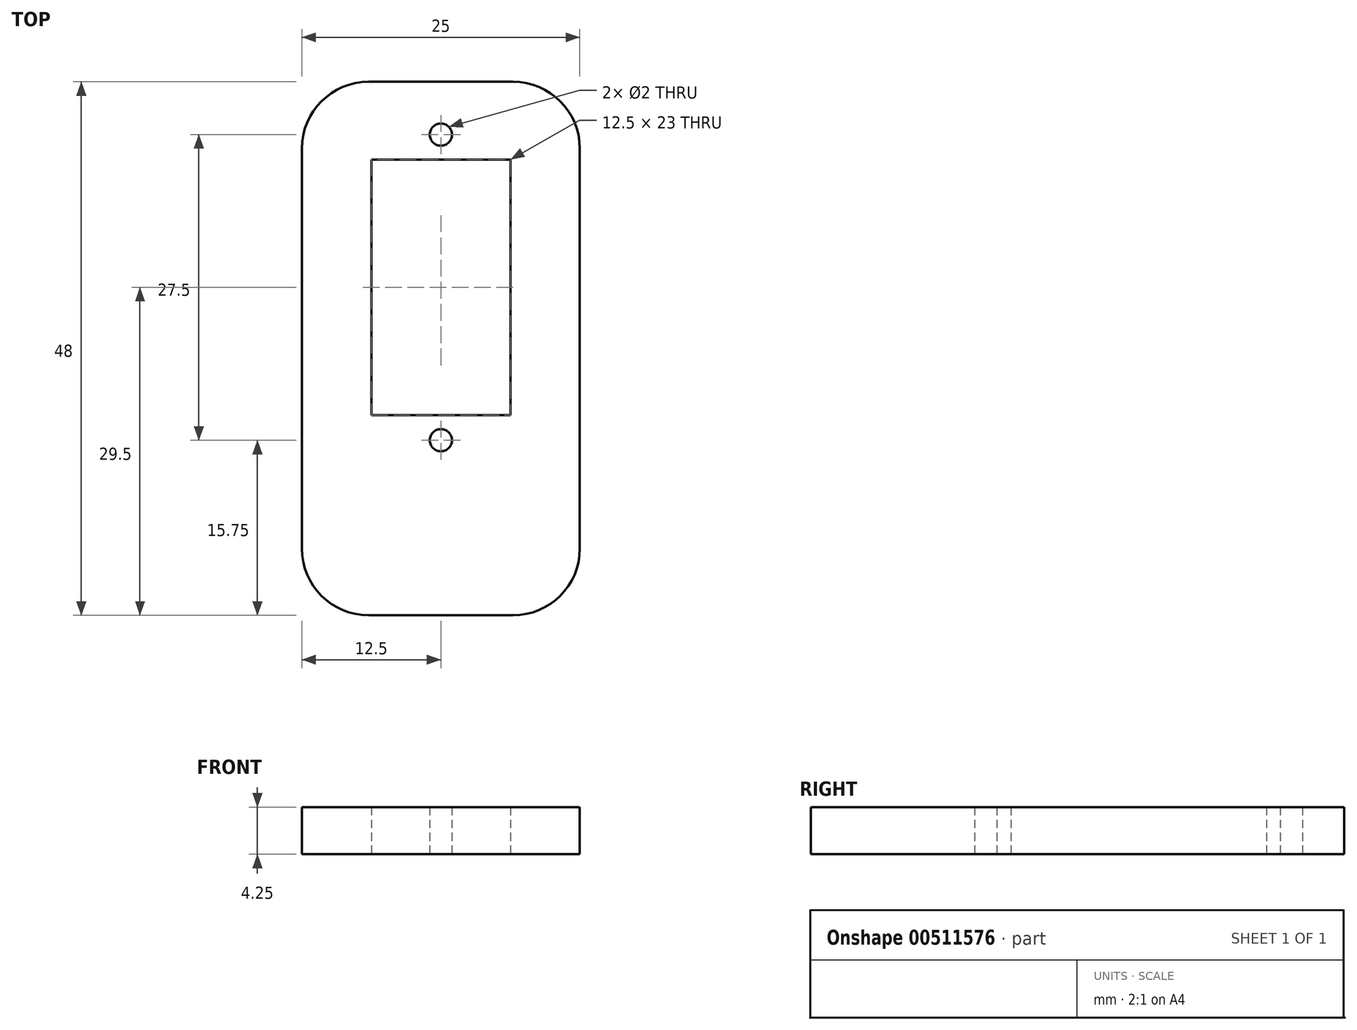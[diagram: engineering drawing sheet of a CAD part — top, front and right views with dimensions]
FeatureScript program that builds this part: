
annotation { "Feature Type Name" : "Feature", "Feature Type Description" : "" }
export const myFeature = defineFeature(function(context is Context, id is Id, definition is map)
    precondition{}
    {
        {
            var Q0;
            Q0=qCreatedBy(makeId("Top.planeOp"),FACE);
            var sketch = newSketch(context, id + "F0", { "sketchPlane" : qUnion([Q0])});
            skLineSegment(sketch, "E0.bottom", {"start": v(6.25, -11.5) * mm, "end": v(-6.25, -11.5) * mm});
            skLineSegment(sketch, "E0.top", {"start": v(6.25, 11.5) * mm, "end": v(-6.25, 11.5) * mm});
            skLineSegment(sketch, "E0.left", {"start": v(6.25, -11.5) * mm, "end": v(6.25, 11.5) * mm});
            skLineSegment(sketch, "E0.right", {"start": v(-6.25, -11.5) * mm, "end": v(-6.25, 11.5) * mm});
            skPoint(sketch, "E0.middle", {"position": v(0, 0) * mm});
            skLineSegment(sketch, "E1.bottom", {"start": v(12.5, -29.5) * mm, "end": v(-12.5, -29.5) * mm});
            skLineSegment(sketch, "E1.top", {"start": v(12.5, 18.5) * mm, "end": v(-12.5, 18.5) * mm});
            skLineSegment(sketch, "E1.left", {"start": v(12.5, -29.5) * mm, "end": v(12.5, 18.5) * mm});
            skLineSegment(sketch, "E1.right", {"start": v(-12.5, -29.5) * mm, "end": v(-12.5, 18.5) * mm});
            skPoint(sketch, "E1.middle", {"position": v(0, -5.5) * mm});
            skLineSegment(sketch, "E2", {"start": v(0, 13.75) * mm, "end": v(0, -13.75) * mm, "construction": true});
            skCircle(sketch, "E3", {"center": v(0, 13.75) * mm, "radius": 1 * mm});
            skCircle(sketch, "E4", {"center": v(0, -13.75) * mm, "radius": 1 * mm});
            skSolve(sketch);
        }
        {
            var Q0;
            Q0=makeQuery(id+"F0.imprint","IMPRINT",FACE,{"disambiguationData":[TD([[makeQuery(id+"F0.imprint","IMPRINT",EDGE,{"derivedFrom":sQuery(id+"F0.wireOp",EDGE,"E0.bottom")}),1.0]])]});
            extrude(context, id + "F1", {"entities" : qUnion([Q0]), "depth" : 4.25 * mm});
        }
        {
            var Q0;
            Q0=makeQuery(id+"F1.opExtrude","SWEPT_EDGE",EDGE,{"disambiguationData":[OSD([sQuery(id+"F0.wireOp",EDGE,"E1.top"),sQuery(id+"F0.wireOp",EDGE,"E1.right")])]});
            var Q1;
            Q1=makeQuery(id+"F1.opExtrude","SWEPT_EDGE",EDGE,{"disambiguationData":[OSD([sQuery(id+"F0.wireOp",EDGE,"E1.top"),sQuery(id+"F0.wireOp",EDGE,"E1.left")])]});
            var Q2;
            Q2=makeQuery(id+"F1.opExtrude","SWEPT_EDGE",EDGE,{"disambiguationData":[OSD([sQuery(id+"F0.wireOp",EDGE,"E1.bottom"),sQuery(id+"F0.wireOp",EDGE,"E1.left")])]});
            var Q3;
            Q3=makeQuery(id+"F1.opExtrude","SWEPT_EDGE",EDGE,{"disambiguationData":[OSD([sQuery(id+"F0.wireOp",EDGE,"E1.bottom"),sQuery(id+"F0.wireOp",EDGE,"E1.right")])]});
            fillet(context, id + "F2", {"entities" : qUnion([Q0, Q1, Q2, Q3]), "radius" : 6 * mm, "tangentPropagation" : true, "allowEdgeOverflow" : false});
        }
    });
